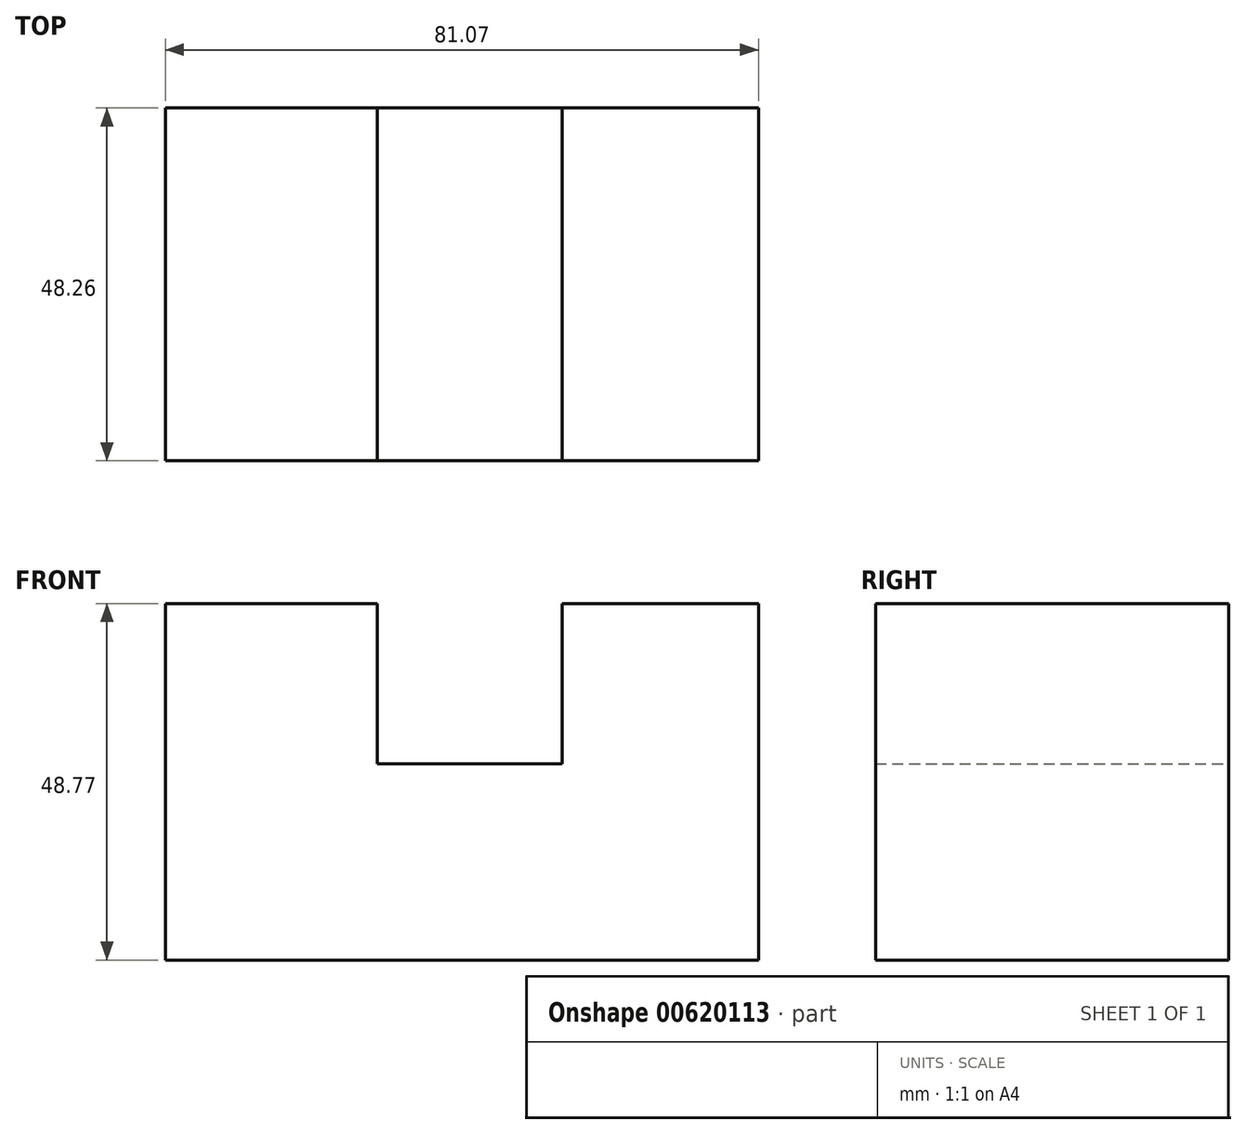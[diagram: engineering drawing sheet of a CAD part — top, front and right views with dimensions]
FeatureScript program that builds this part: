
annotation { "Feature Type Name" : "Feature", "Feature Type Description" : "" }
export const myFeature = defineFeature(function(context is Context, id is Id, definition is map)
    precondition{}
    {
        {
            var Q0;
            Q0=qCreatedBy(makeId("Front.planeOp"),FACE);
            var sketch = newSketch(context, id + "F0", { "sketchPlane" : qUnion([Q0])});
            skLineSegment(sketch, "E0", {"start": v(-66.9, 48.77) * mm, "end": v(-37.95, 48.77) * mm});
            skLineSegment(sketch, "E1", {"start": v(-37.95, 48.77) * mm, "end": v(-37.95, 26.82) * mm});
            skLineSegment(sketch, "E2", {"start": v(-37.95, 26.82) * mm, "end": v(-12.65, 26.82) * mm});
            skLineSegment(sketch, "E3", {"start": v(-12.65, 26.82) * mm, "end": v(-12.65, 48.77) * mm});
            skLineSegment(sketch, "E4", {"start": v(-12.65, 48.77) * mm, "end": v(14.17, 48.77) * mm});
            skLineSegment(sketch, "E5", {"start": v(14.17, 48.77) * mm, "end": v(14.17, 0) * mm});
            skLineSegment(sketch, "E6", {"start": v(-66.9, 48.77) * mm, "end": v(-66.9, 0) * mm});
            skLineSegment(sketch, "E7", {"start": v(-66.9, 0) * mm, "end": v(14.17, 0) * mm});
            skSolve(sketch);
        }
        {
            var Q0;
            Q0 = qSketchRegion(id + "F0", true);
            extrude(context, id + "F1", {"entities" : qUnion([Q0]), "depth" : 48.26 * mm, "offsetDistance" : 25.4 * mm});
        }
    });
